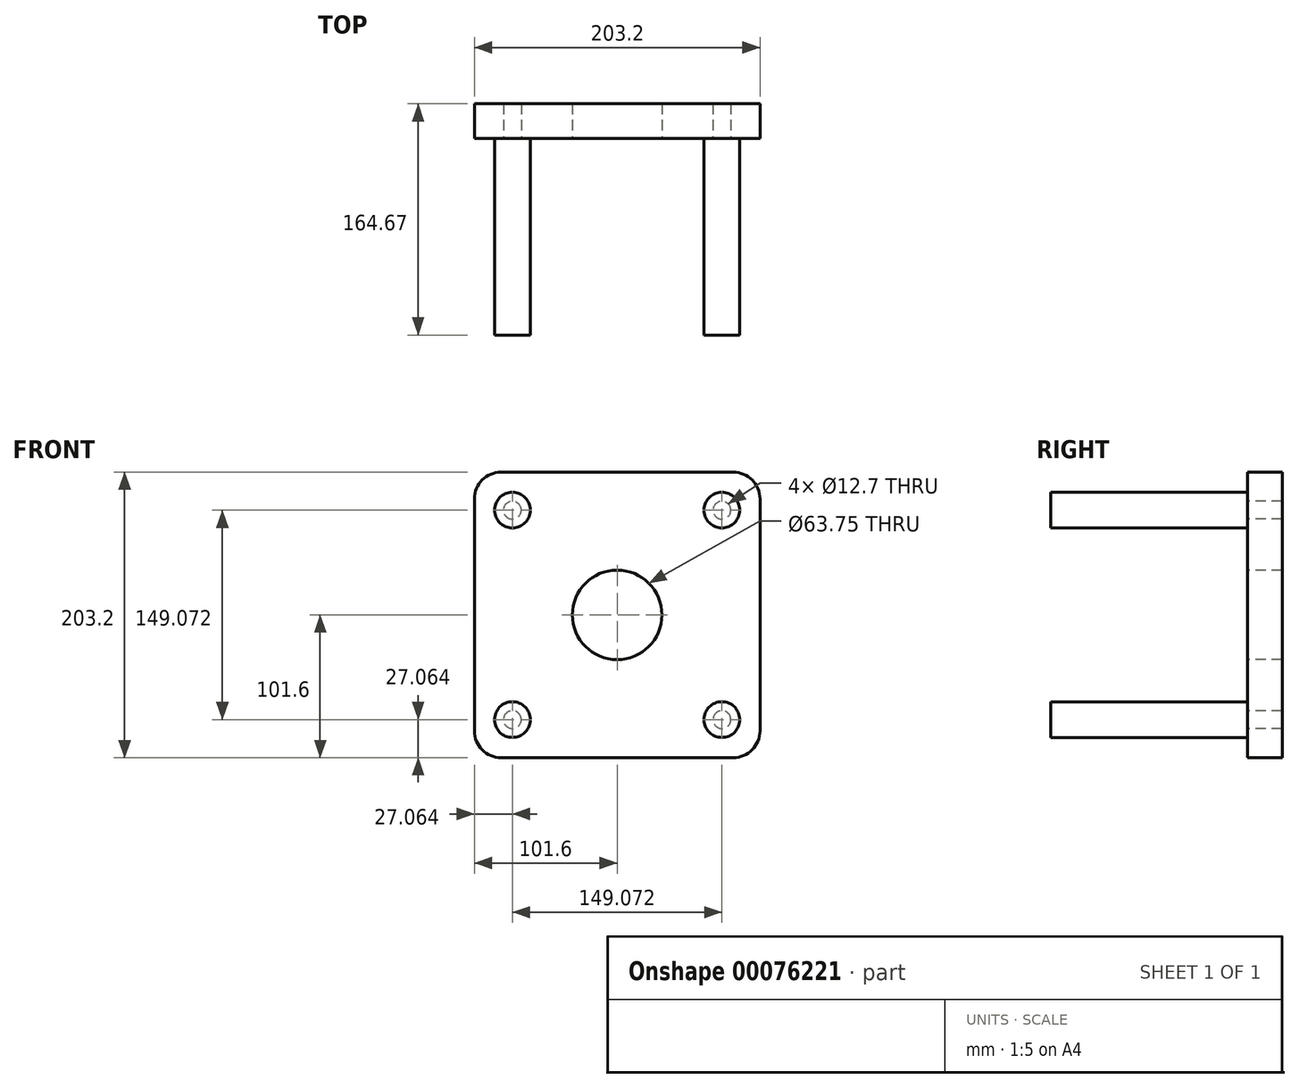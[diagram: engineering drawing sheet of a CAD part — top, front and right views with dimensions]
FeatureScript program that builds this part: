
annotation { "Feature Type Name" : "Feature", "Feature Type Description" : "" }
export const myFeature = defineFeature(function(context is Context, id is Id, definition is map)
    precondition{}
    {
        {
            var Q0;
            Q0=qCreatedBy(makeId("Front.planeOp"),FACE);
            var sketch = newSketch(context, id + "F0", { "sketchPlane" : qUnion([Q0])});
            skLineSegment(sketch, "E0.bottom", {"start": v(101.6, -101.6) * mm, "end": v(-101.6, -101.6) * mm});
            skLineSegment(sketch, "E0.top", {"start": v(101.6, 101.6) * mm, "end": v(-101.6, 101.6) * mm});
            skLineSegment(sketch, "E0.left", {"start": v(101.6, -101.6) * mm, "end": v(101.6, 101.6) * mm});
            skLineSegment(sketch, "E0.right", {"start": v(-101.6, -101.6) * mm, "end": v(-101.6, 101.6) * mm});
            skPoint(sketch, "E0.middle", {"position": v(0, 0) * mm});
            skSolve(sketch);
        }
        {
            var Q0;
            Q0 = qSketchRegion(id + "F0", true);
            extrude(context, id + "F1", {"entities" : qUnion([Q0]), "oppositeDirection" : true, "depth" : 24.59 * mm});
        }
        {
            var Q0;
            Q0=makeQuery(id+"F1.opExtrude","SWEPT_EDGE",EDGE,{"disambiguationData":[OSD([sQuery(id+"F0.wireOp",EDGE,"E0.top"),sQuery(id+"F0.wireOp",EDGE,"E0.right")])]});
            var Q1;
            Q1=makeQuery(id+"F1.opExtrude","SWEPT_EDGE",EDGE,{"disambiguationData":[OSD([sQuery(id+"F0.wireOp",EDGE,"E0.top"),sQuery(id+"F0.wireOp",EDGE,"E0.left")])]});
            var Q2;
            Q2=makeQuery(id+"F1.opExtrude","SWEPT_EDGE",EDGE,{"disambiguationData":[OSD([sQuery(id+"F0.wireOp",EDGE,"E0.bottom"),sQuery(id+"F0.wireOp",EDGE,"E0.right")])]});
            var Q3;
            Q3=makeQuery(id+"F1.opExtrude","SWEPT_EDGE",EDGE,{"disambiguationData":[OSD([sQuery(id+"F0.wireOp",EDGE,"E0.bottom"),sQuery(id+"F0.wireOp",EDGE,"E0.left")])]});
            fillet(context, id + "F2", {"entities" : qUnion([Q0, Q1, Q2, Q3]), "radius" : 19.05 * mm, "tangentPropagation" : true, "allowEdgeOverflow" : false});
        }
        {
            var Q0;
            Q0=makeQuery(id+"F1.opExtrude","CAP_FACE",FACE,{"disambiguationData":[OSD([sQuery(id+"F0.wireOp",EDGE,"E0.bottom"),sQuery(id+"F0.wireOp",EDGE,"E0.top"),sQuery(id+"F0.wireOp",EDGE,"E0.left"),sQuery(id+"F0.wireOp",EDGE,"E0.right")])],"isStart":true});
            var sketch = newSketch(context, id + "F3", { "sketchPlane" : qUnion([Q0])});
            skCircle(sketch, "E1", {"center": v(0, 0) * mm, "radius": 31.88 * mm});
            skSolve(sketch);
        }
        {
            var Q0;
            Q0 = qSketchRegion(id + "F3", true);
            extrude(context, id + "F4", {"entities" : qUnion([Q0]), "operationType" : NewBodyOperationType.REMOVE, "endBound" : BoundingType.THROUGH_ALL, "oppositeDirection" : true, "depth" : 25.4 * mm});
        }
        {
            var Q0;
            Q0=makeQuery(id+"F1.opExtrude","CAP_FACE",FACE,{"disambiguationData":[OSD([sQuery(id+"F0.wireOp",EDGE,"E0.bottom"),sQuery(id+"F0.wireOp",EDGE,"E0.top"),sQuery(id+"F0.wireOp",EDGE,"E0.left"),sQuery(id+"F0.wireOp",EDGE,"E0.right")])],"isStart":true});
            var sketch = newSketch(context, id + "F5", { "sketchPlane" : qUnion([Q0])});
            skLineSegment(sketch, "E2", {"start": v(-96.02, 96.02) * mm, "end": v(96.02, -96.02) * mm, "construction": true});
            skLineSegment(sketch, "E3", {"start": v(96.02, 96.02) * mm, "end": v(-96.02, -96.02) * mm, "construction": true});
            skPoint(sketch, "E4", {"position": v(-74.54, 74.54) * mm});
            skPoint(sketch, "E5", {"position": v(74.54, 74.54) * mm});
            skPoint(sketch, "E6", {"position": v(-74.54, -74.54) * mm});
            skPoint(sketch, "E7", {"position": v(74.54, -74.54) * mm});
            skPoint(sketch, "E8", {"position": v(-22.54, 22.54) * mm});
            skPoint(sketch, "E9", {"position": v(-22.54, -22.54) * mm});
            skPoint(sketch, "E10", {"position": v(22.54, 22.54) * mm});
            skSolve(sketch);
        }
        {
            var Q0;
            Q0=sQuery(id+"F5.wireOp",VERTEX,"E4");
            var Q1;
            Q1=sQuery(id+"F5.wireOp",VERTEX,"E5");
            var Q2;
            Q2=sQuery(id+"F5.wireOp",VERTEX,"E7");
            var Q3;
            Q3=sQuery(id+"F5.wireOp",VERTEX,"E6");
            var Q4;
            Q4=makeQuery(id+"F1.opExtrude","SWEPT_BODY",BODY,{"disambiguationData":[OSD([sQuery(id+"F0.wireOp",EDGE,"E0.bottom"),sQuery(id+"F0.wireOp",EDGE,"E0.top"),sQuery(id+"F0.wireOp",EDGE,"E0.left"),sQuery(id+"F0.wireOp",EDGE,"E0.right")])]});
            hole(context, id + "F6", {"style" : HoleStyle.SIMPLE, "endStyle" : HoleEndStyle.THROUGH, "holeDiameter" : 12.7 * mm, "locations" : qUnion([Q0, Q1, Q2, Q3]), "scope" : qUnion([Q4]), "isTappedThrough" : true});
        }
        {
            var Q0;
            Q0=makeQuery(id+"F1.opExtrude","CAP_FACE",FACE,{"disambiguationData":[OSD([sQuery(id+"F0.wireOp",EDGE,"E0.bottom"),sQuery(id+"F0.wireOp",EDGE,"E0.top"),sQuery(id+"F0.wireOp",EDGE,"E0.left"),sQuery(id+"F0.wireOp",EDGE,"E0.right")])],"isStart":true});
            var sketch = newSketch(context, id + "F7", { "sketchPlane" : qUnion([Q0])});
            skCircle(sketch, "E11", {"center": v(-74.54, 74.54) * mm, "radius": 12.7 * mm});
            skCircle(sketch, "E12", {"center": v(-74.54, -74.54) * mm, "radius": 12.7 * mm});
            skCircle(sketch, "E13", {"center": v(74.54, -74.54) * mm, "radius": 12.7 * mm});
            skCircle(sketch, "E14", {"center": v(74.54, 74.54) * mm, "radius": 12.7 * mm});
            skSolve(sketch);
        }
        {
            var Q0;
            Q0 = qSketchRegion(id + "F7", true);
            extrude(context, id + "F8", {"entities" : qUnion([Q0]), "depth" : 140.08 * mm});
        }
    });
